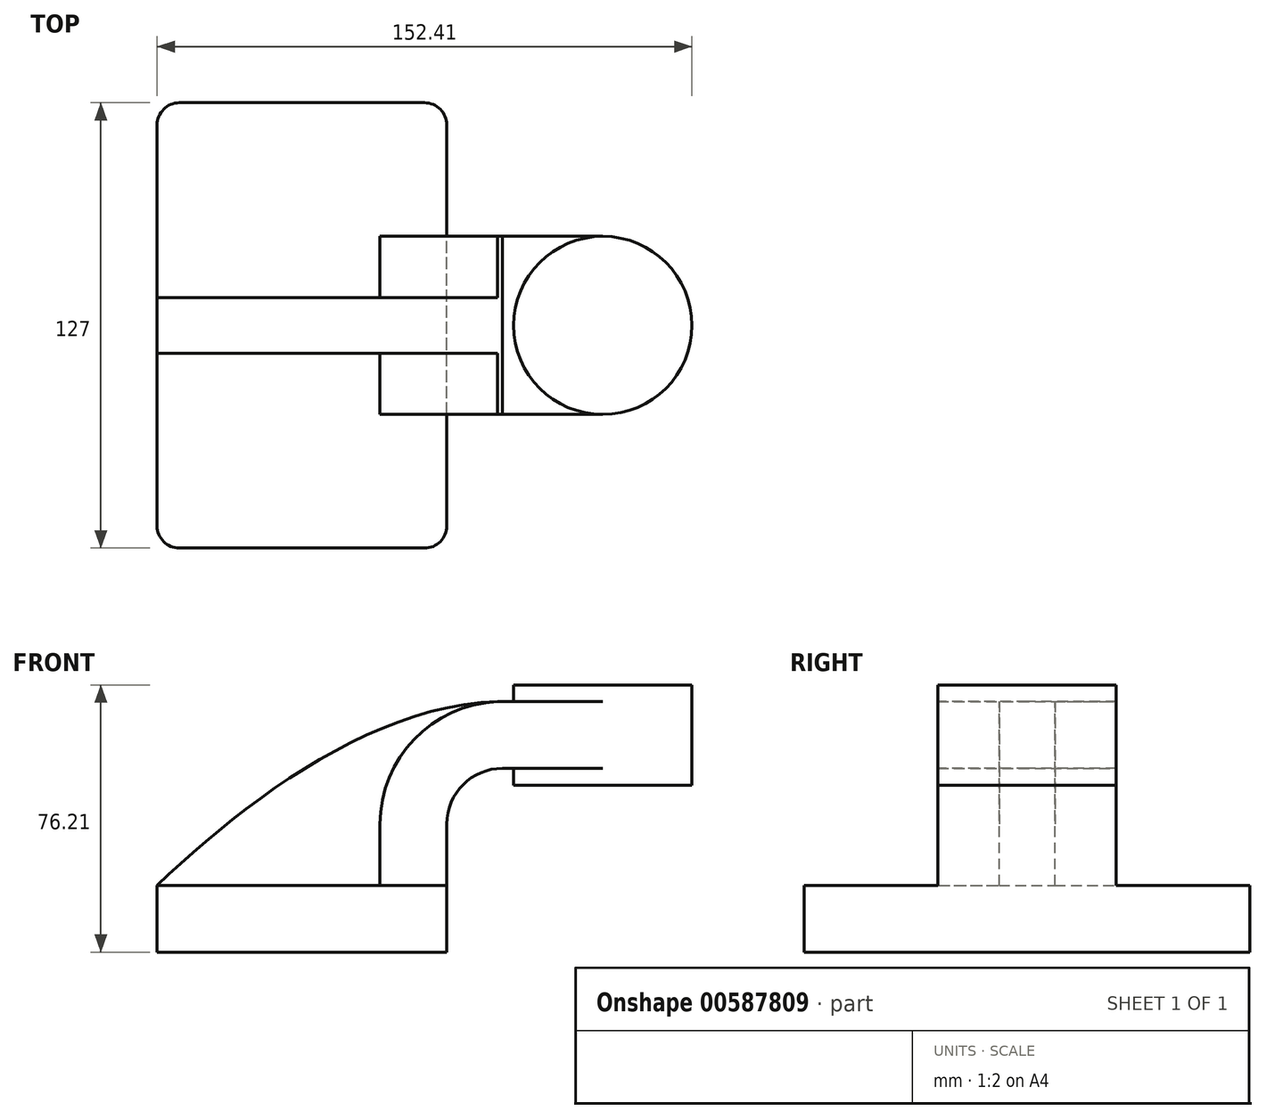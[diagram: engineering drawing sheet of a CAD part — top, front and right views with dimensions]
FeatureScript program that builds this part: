
annotation { "Feature Type Name" : "Feature", "Feature Type Description" : "" }
export const myFeature = defineFeature(function(context is Context, id is Id, definition is map)
    precondition{}
    {
        {
            var Q0;
            Q0=qCreatedBy(makeId("Front.planeOp"),FACE);
            var sketch = newSketch(context, id + "F0", { "sketchPlane" : qUnion([Q0])});
            skLineSegment(sketch, "E0.bottom", {"start": v(-41.28, 9.52) * mm, "end": v(41.27, 9.53) * mm});
            skLineSegment(sketch, "E0.top", {"start": v(-41.28, -9.53) * mm, "end": v(41.28, -9.53) * mm});
            skLineSegment(sketch, "E0.left", {"start": v(-41.28, 9.52) * mm, "end": v(-41.27, -9.53) * mm});
            skLineSegment(sketch, "E0.right", {"start": v(41.28, 9.53) * mm, "end": v(41.28, -9.52) * mm});
            skPoint(sketch, "E0.middle", {"position": v(0, 0) * mm});
            skLineSegment(sketch, "E1.bottom", {"start": v(60.32, 38.1) * mm, "end": v(111.12, 38.1) * mm});
            skLineSegment(sketch, "E1.top", {"start": v(60.32, 66.68) * mm, "end": v(111.12, 66.68) * mm});
            skLineSegment(sketch, "E1.left", {"start": v(60.32, 38.1) * mm, "end": v(60.32, 66.68) * mm});
            skLineSegment(sketch, "E1.right", {"start": v(111.12, 38.1) * mm, "end": v(111.12, 66.68) * mm});
            skPoint(sketch, "E1.middle", {"position": v(85.72, 52.39) * mm});
            skLineSegment(sketch, "E2", {"start": v(41.27, 9.53) * mm, "end": v(41.27, 27) * mm});
            skArc(sketch, "E3", {"start": v(41.27, 27) * mm, "mid": v(45.92, 38.23) * mm, "end": v(57.15, 42.88) * mm});
            skLineSegment(sketch, "E4", {"start": v(57.15, 42.88) * mm, "end": v(85.72, 42.88) * mm});
            skLineSegment(sketch, "E5.0", {"start": v(57.15, 61.93) * mm, "end": v(85.72, 61.93) * mm});
            skArc(sketch, "E5.1", {"start": v(22.23, 27) * mm, "mid": v(32.45, 51.7) * mm, "end": v(57.15, 61.93) * mm});
            skLineSegment(sketch, "E5.2", {"start": v(22.22, 9.53) * mm, "end": v(22.22, 27) * mm});
            skLineSegment(sketch, "E6", {"start": v(85.72, 38.1) * mm, "end": v(85.72, 66.68) * mm});
            skFitSpline(sketch, "E7", {"points": [v(-41.28, 9.52) * mm, v(57.15, 61.93) * mm], "startDerivative": vector(75.37, 71.43) * mm, "endDerivative": vector(110.66, 1.19) * mm});
            skSolve(sketch);
        }
        {
            var Q0;
            Q0=makeQuery(id+"F0.imprint","IMPRINT",FACE,{"disambiguationData":[TD([[makeQuery(id+"F0.imprint","IMPRINT",EDGE,{"derivedFrom":sQuery(id+"F0.wireOp",EDGE,"E0.top")}),1.0]])]});
            extrude(context, id + "F1", {"entities" : qUnion([Q0]), "endBound" : BoundingType.SYMMETRIC, "depth" : 127 * mm, "offsetDistance" : 25.4 * mm});
        }
        {
            var Q0;
            {var subQ1=sQuery(id+"F0.wireOp",EDGE,"E2");Q0=makeQuery(id+"F0.imprint","IMPRINT",FACE,{"disambiguationData":[TD([[makeQuery(id+"F0.imprint","IMPRINT",EDGE,{"derivedFrom":subQ1}),1.0]])]});}
            extrude(context, id + "F2", {"entities" : qUnion([Q0]), "operationType" : NewBodyOperationType.ADD, "endBound" : BoundingType.SYMMETRIC, "depth" : 50.8 * mm, "offsetDistance" : 25.4 * mm});
        }
        {
            var Q0;
            {var subQ3=sQuery(id+"F0.wireOp",EDGE,"E5.2");Q0=makeQuery(id+"F0.imprint","IMPRINT",FACE,{"disambiguationData":[TD([[makeQuery(id+"F0.imprint","IMPRINT",EDGE,{"derivedFrom":subQ3}),1.0]])]});}
            extrude(context, id + "F3", {"entities" : qUnion([Q0]), "operationType" : NewBodyOperationType.ADD, "endBound" : BoundingType.SYMMETRIC, "depth" : 15.88 * mm, "offsetDistance" : 25.4 * mm});
        }
        {
            var Q0;
            {var subQ0=sQuery(id+"F0.wireOp",EDGE,"E4");var subQ1=sQuery(id+"F0.wireOp",EDGE,"E1.left");var subQ2=makeQuery(id+"F0.imprint","INTERSECT",VERTEX,{"derivedFrom":[subQ1,subQ0]});Q0=makeQuery(id+"F0.imprint","IMPRINT",FACE,{"disambiguationData":[TD([[makeQuery(id+"F0.imprint","IMPRINT",EDGE,{"disambiguationData":[TD([[subQ2,-1.0]])],"derivedFrom":subQ1}),-1.0]])]});}
            extrude(context, id + "F4", {"entities" : qUnion([Q0]), "operationType" : NewBodyOperationType.ADD, "endBound" : BoundingType.SYMMETRIC, "depth" : 50.8 * mm, "offsetDistance" : 25.4 * mm});
        }
        {
            var Q0;
            {var subQ4=sQuery(id+"F0.wireOp",EDGE,"E1.right");Q0=makeQuery(id+"F0.imprint","IMPRINT",FACE,{"disambiguationData":[TD([[makeQuery(id+"F0.imprint","IMPRINT",EDGE,{"derivedFrom":subQ4}),1.0]])]});}
            var Q1;
            Q1=sQuery(id+"F0.wireOp",EDGE,"E6");
            revolve(context, id + "F5", {"operationType" : NewBodyOperationType.ADD, "entities" : qUnion([Q0]), "axis" : qUnion([Q1]), "revolveType" : RevolveType.FULL});
        }
        {
            var Q0;
            Q0=makeQuery(id+"F1.opExtrude","CAP_EDGE",EDGE,{"disambiguationData":[OSD([sQuery(id+"F0.wireOp",EDGE,"E0.right")])],"isStart":false});
            var Q1;
            Q1=makeQuery(id+"F1.opExtrude","CAP_EDGE",EDGE,{"disambiguationData":[OSD([sQuery(id+"F0.wireOp",EDGE,"E0.left")])],"isStart":false});
            var Q2;
            Q2=makeQuery(id+"F1.opExtrude","CAP_EDGE",EDGE,{"disambiguationData":[OSD([sQuery(id+"F0.wireOp",EDGE,"E0.right")])],"isStart":true});
            var Q3;
            Q3=makeQuery(id+"F1.opExtrude","CAP_EDGE",EDGE,{"disambiguationData":[OSD([sQuery(id+"F0.wireOp",EDGE,"E0.left")])],"isStart":true});
            fillet(context, id + "F6", {"entities" : qUnion([Q0, Q1, Q2, Q3]), "radius" : 6.35 * mm, "tangentPropagation" : true, "allowEdgeOverflow" : false});
        }
    });
